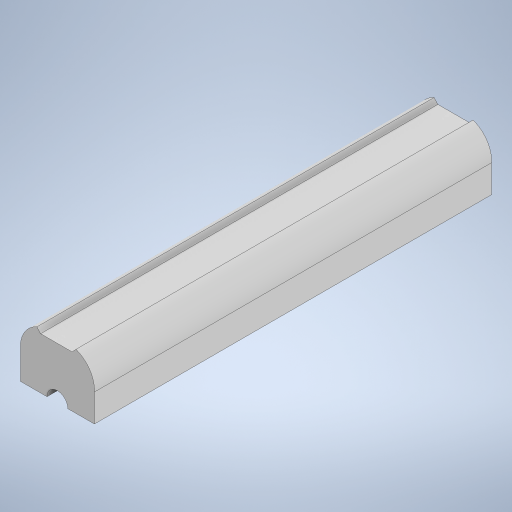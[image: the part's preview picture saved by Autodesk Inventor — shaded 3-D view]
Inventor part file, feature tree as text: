
AUTODESK INVENTOR PART (.ipt)
format: ipt  version: 2023 (Build 270158000, 158)  size: 237,056 bytes
history: native  units: in
note: dims shown in document units (in); Inventor stores cm internally (conversion verified against a paired STEP export)
features: extrude x1, sketch x1
ambient origin geometry x8: Origin, YZ Plane, XZ Plane, XY Plane, X Axis, Y Axis, Z Axis, Center Point
bodies: Solid1 (feature_tree)
feature tree (2):
  extrude  "Extrusion1"  Depth=1.1811in
  sketch  "Sketch1"  dims[d0=1.5748in d1=1.1811in d2=1.5748in d3=1.1811in d4=1.1811in d5=2.3622in d7=0.2362in d9=0.7874in d10=0.8858in d11=16.9291in d12=0.0in d13=0.0344in d14=0.0344in]
